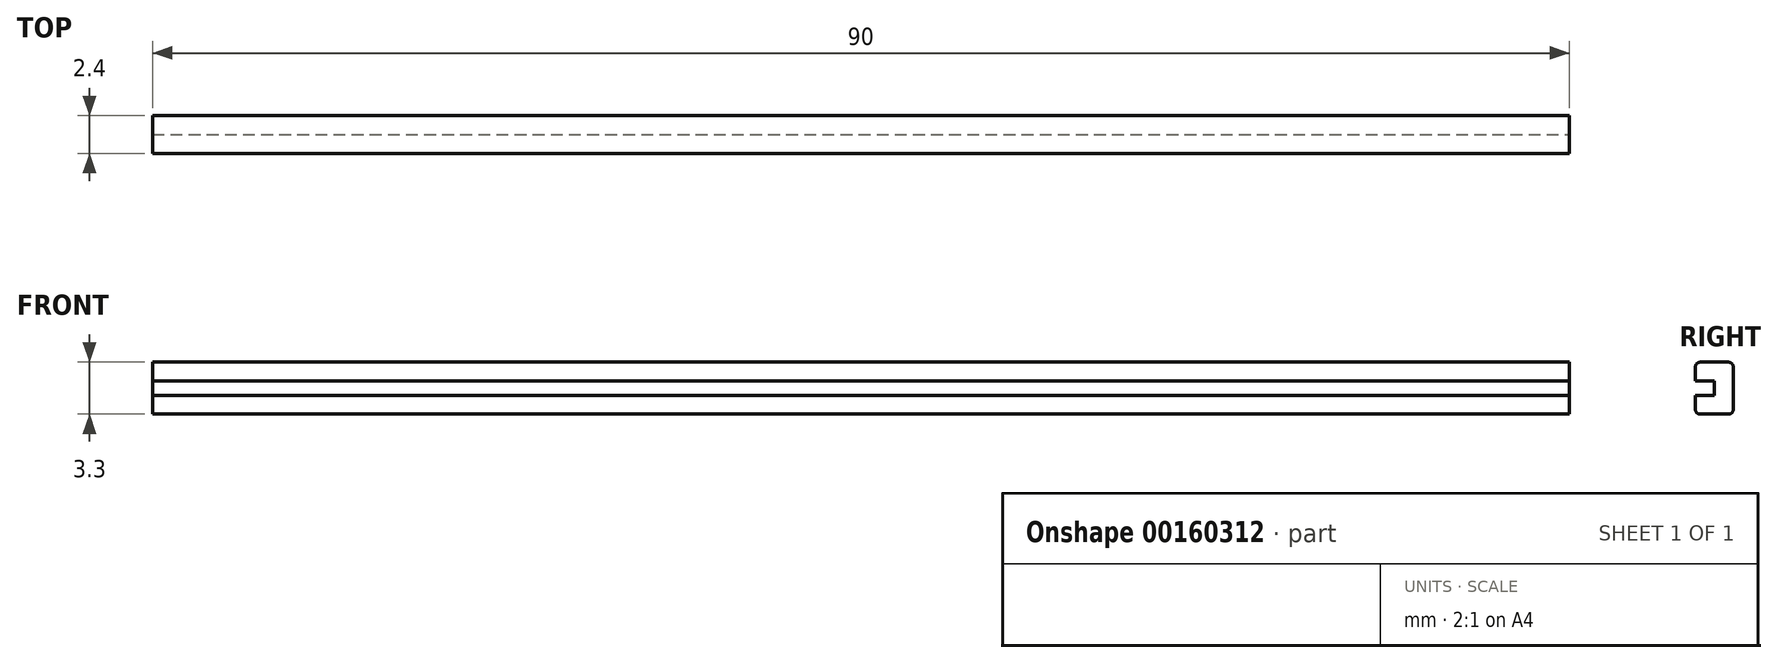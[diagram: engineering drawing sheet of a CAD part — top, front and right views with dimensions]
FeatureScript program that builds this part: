
annotation { "Feature Type Name" : "Feature", "Feature Type Description" : "" }
export const myFeature = defineFeature(function(context is Context, id is Id, definition is map)
    precondition{}
    {
        {
            var Q0;
            Q0=qCreatedBy(makeId("Front.planeOp"),FACE);
            var sketch = newSketch(context, id + "F0", { "sketchPlane" : qUnion([Q0])});
            skLineSegment(sketch, "E0.bottom", {"start": v(0, 0) * mm, "end": v(90, 0) * mm});
            skLineSegment(sketch, "E0.top", {"start": v(0, 3.3) * mm, "end": v(90, 3.3) * mm});
            skLineSegment(sketch, "E0.left", {"start": v(0, 0) * mm, "end": v(0, 3.3) * mm});
            skLineSegment(sketch, "E0.right", {"start": v(90, 0) * mm, "end": v(90, 3.3) * mm});
            skSolve(sketch);
        }
        {
            var Q0;
            Q0 = qSketchRegion(id + "F0", true);
            extrude(context, id + "F1", {"entities" : qUnion([Q0]), "depth" : 2.4 * mm});
        }
        {
            var Q0;
            Q0=makeQuery(id+"F1.opExtrude","CAP_FACE",FACE,{"disambiguationData":[OSD([sQuery(id+"F0.wireOp",EDGE,"E0.bottom"),sQuery(id+"F0.wireOp",EDGE,"E0.top"),sQuery(id+"F0.wireOp",EDGE,"E0.left"),sQuery(id+"F0.wireOp",EDGE,"E0.right")])],"isStart":false});
            var Q1;
            Q1=makeQuery(id+"F1.opExtrude","SWEPT_FACE",FACE,{"disambiguationData":[OSD([sQuery(id+"F0.wireOp",EDGE,"E0.right")])]});
            var Q2;
            Q2=makeQuery(id+"F1.opExtrude","SWEPT_FACE",FACE,{"disambiguationData":[OSD([sQuery(id+"F0.wireOp",EDGE,"E0.left")])]});
            shell(context, id + "F2", {"entities" : qUnion([Q0, Q1, Q2]), "thickness" : 1.2 * mm});
        }
        {
            var Q0;
            Q0=makeQuery(id+"F1.opExtrude","CAP_EDGE",EDGE,{"disambiguationData":[OSD([sQuery(id+"F0.wireOp",EDGE,"E0.top")])],"isStart":false});
            var Q1;
            Q1=makeQuery(id+"F1.opExtrude","CAP_EDGE",EDGE,{"disambiguationData":[OSD([sQuery(id+"F0.wireOp",EDGE,"E0.top")])],"isStart":true});
            var Q2;
            Q2=makeQuery(id+"F1.opExtrude","CAP_EDGE",EDGE,{"disambiguationData":[OSD([sQuery(id+"F0.wireOp",EDGE,"E0.bottom")])],"isStart":false});
            var Q3;
            Q3=makeQuery(id+"F1.opExtrude","CAP_EDGE",EDGE,{"disambiguationData":[OSD([sQuery(id+"F0.wireOp",EDGE,"E0.bottom")])],"isStart":true});
            fillet(context, id + "F3", {"entities" : qUnion([Q0, Q1, Q2, Q3]), "radius" : .3 * mm, "tangentPropagation" : true, "allowEdgeOverflow" : false});
        }
    });
